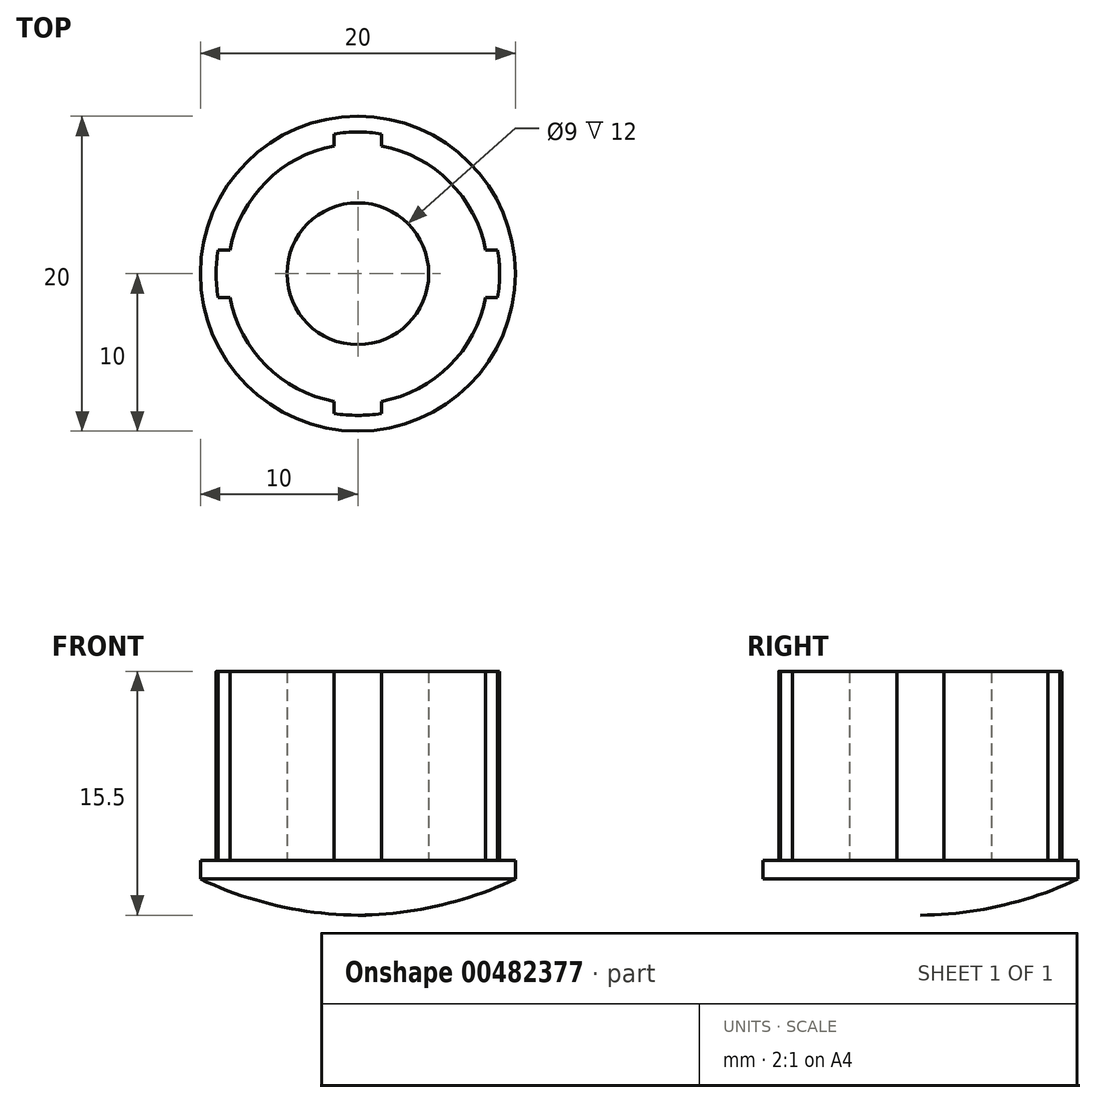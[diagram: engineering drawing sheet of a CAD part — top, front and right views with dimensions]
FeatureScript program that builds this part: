
annotation { "Feature Type Name" : "Feature", "Feature Type Description" : "" }
export const myFeature = defineFeature(function(context is Context, id is Id, definition is map)
    precondition{}
    {
        {
            var Q0;
            Q0=qCreatedBy(makeId("Top.planeOp"),FACE);
            var sketch = newSketch(context, id + "F0", { "sketchPlane" : qUnion([Q0])});
            skCircle(sketch, "E0", {"center": v(0, 0) * mm, "radius": 9 * mm, "construction": true});
            skCircle(sketch, "E1", {"center": v(0, 0) * mm, "radius": 4.5 * mm});
            skCircle(sketch, "E2", {"center": v(0, 0) * mm, "radius": 8.25 * mm});
            skLineSegment(sketch, "E3", {"start": v(-8.87, 1.5) * mm, "end": v(-8.11, 1.5) * mm});
            skLineSegment(sketch, "E4.MirrorCS", {"start": v(-8.87, -1.5) * mm, "end": v(-8.11, -1.5) * mm});
            skArc(sketch, "E5", {"start": v(-8.87, -1.5) * mm, "mid": v(-9, 0) * mm, "end": v(-8.87, 1.5) * mm});
            skLineSegment(sketch, "E6.MirrorCS", {"start": v(8.87, 1.5) * mm, "end": v(8.11, 1.5) * mm});
            skArc(sketch, "E7.MirrorCS", {"start": v(8.87, -1.5) * mm, "mid": v(9, 0) * mm, "end": v(8.87, 1.5) * mm});
            skLineSegment(sketch, "E8.MirrorCS", {"start": v(8.87, -1.5) * mm, "end": v(8.11, -1.5) * mm});
            skLineSegment(sketch, "E9", {"start": v(-1.5, 8.87) * mm, "end": v(-1.5, 8.11) * mm});
            skLineSegment(sketch, "E10.MirrorCS", {"start": v(1.5, 8.87) * mm, "end": v(1.5, 8.11) * mm});
            skArc(sketch, "E11", {"start": v(-1.5, 8.87) * mm, "mid": v(0, 9) * mm, "end": v(1.5, 8.87) * mm});
            skArc(sketch, "E12.MirrorCS", {"start": v(-1.5, -8.87) * mm, "mid": v(0, -9) * mm, "end": v(1.5, -8.87) * mm});
            skLineSegment(sketch, "E13.MirrorCS", {"start": v(-1.5, -8.87) * mm, "end": v(-1.5, -8.11) * mm});
            skLineSegment(sketch, "E14.MirrorCS", {"start": v(1.5, -8.87) * mm, "end": v(1.5, -8.11) * mm});
            skSolve(sketch);
        }
        {
            var Q0;
            {var subQ0=sQuery(id+"F0.wireOp",EDGE,"E3");Q0=makeQuery(id+"F0.imprint","IMPRINT",FACE,{"disambiguationData":[TD([[makeQuery(id+"F0.imprint","IMPRINT",EDGE,{"derivedFrom":subQ0}),-1.0]])]});}
            var Q1;
            Q1=makeQuery(id+"F0.imprint","IMPRINT",FACE,{"disambiguationData":[TD([[makeQuery(id+"F0.imprint","IMPRINT",EDGE,{"derivedFrom":sQuery(id+"F0.wireOp",EDGE,"E1")}),-1.0]])]});
            var Q2;
            {var subQ0=sQuery(id+"F0.wireOp",EDGE,"E9");Q2=makeQuery(id+"F0.imprint","IMPRINT",FACE,{"disambiguationData":[TD([[makeQuery(id+"F0.imprint","IMPRINT",EDGE,{"derivedFrom":subQ0}),1.0]])]});}
            var Q3;
            {var subQ0=sQuery(id+"F0.wireOp",EDGE,"E6.MirrorCS");Q3=makeQuery(id+"F0.imprint","IMPRINT",FACE,{"disambiguationData":[TD([[makeQuery(id+"F0.imprint","IMPRINT",EDGE,{"derivedFrom":subQ0}),1.0]])]});}
            var Q4;
            Q4=makeQuery(id+"F0.imprint","IMPRINT",FACE,{"disambiguationData":[TD([[makeQuery(id+"F0.imprint","IMPRINT",EDGE,{"derivedFrom":sQuery(id+"F0.wireOp",EDGE,"E12.MirrorCS")}),1.0]])]});
            extrude(context, id + "F1", {"entities" : qUnion([Q0, Q1, Q2, Q3, Q4]), "depth" : 12 * mm});
        }
        {
            var Q0;
            Q0=qCreatedBy(makeId("Front.planeOp"),FACE);
            var sketch = newSketch(context, id + "F2", { "sketchPlane" : qUnion([Q0])});
            skLineSegment(sketch, "E15", {"start": v(0, 0) * mm, "end": v(0, -3.5) * mm});
            skLineSegment(sketch, "E16", {"start": v(0, 0) * mm, "end": v(-10, 0) * mm});
            skLineSegment(sketch, "E17", {"start": v(-10, 0) * mm, "end": v(-10, -1.2) * mm});
            skLineSegment(sketch, "E18", {"start": v(0.25, -3.5) * mm, "end": v(0, -3.5) * mm});
            skArc(sketch, "E19", {"start": v(0.25, -3.5) * mm, "mid": v(-5, -2.92) * mm, "end": v(-10, -1.2) * mm});
            skSolve(sketch);
        }
        {
            var Q0;
            Q0=makeQuery(id+"F2.imprint","IMPRINT",FACE,{"disambiguationData":[TD([[makeQuery(id+"F2.imprint","IMPRINT",EDGE,{"derivedFrom":sQuery(id+"F2.wireOp",EDGE,"E15")}),-1.0]])]});
            var Q1;
            Q1=makeQuery(id+"F1.opExtrude","SWEPT_FACE",FACE,{"disambiguationData":[OSD([sQuery(id+"F0.wireOp",EDGE,"E12.MirrorCS")])]});
            revolve(context, id + "F3", {"operationType" : NewBodyOperationType.ADD, "entities" : qUnion([Q0]), "axis" : qUnion([Q1]), "revolveType" : RevolveType.FULL});
        }
    });
